SOLIDWORKS PART (.sldprt)
format: sldprt  version: not decoded by parser v0  size: 160,256 bytes
history: native  units: mm
features: sketch x5, extrude x3, fillet x2, cut_extrude x2, material x1 (+13 scaffold rows collapsed)
feature tree (26):
  scaffold x13  (default folders/planes/origin — collapsed)
  material  "Material <not specified>"
  sketch  "Sketch1"  dims[D1=20.0mm D2=8.0mm D3=8.0mm]
  extrude  "Boss-Extrude1"  Depth=2mm
  fillet  "Fillet1"  Radius=4mm
  sketch  "Sketch2"  dims[D1=3.1mm D2=3.1mm]
  cut_extrude  "Cut-Extrude1"  [1 undecoded]
  sketch  "Sketch3"  dims[c1.D3=~10.515223mm c1.D1=2.0mm c1.D2=2.0mm c2.D3=6.0mm c2.D4=6.0mm c2.D5=6.0mm]
  extrude  "Boss-Extrude2"  Depth=12mm
  sketch  "Sketch4"  dims[c1.D1=8.0mm c1.D2=~5.656854mm c2.D2=150.0deg]
  extrude  "Boss-Extrude3"  [1 undecoded]
  fillet  "Fillet2"  Radius=4mm
  sketch  "Sketch5"  dims[D1=3.1mm D2=3.1mm]
  cut_extrude  "Cut-Extrude2"  [1 undecoded]
decode coverage: 9 of 12 modeling features carry decoded parameters
note: ~ marks probable driven/reference dimensions
note: 3 parameter values undecoded
summary: no parameter record found for 3 features
note: suppression state not decoded; provenance and decode notes live in map.json
